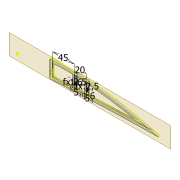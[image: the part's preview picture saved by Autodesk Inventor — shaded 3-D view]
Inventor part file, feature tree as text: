
AUTODESK INVENTOR PART (.ipt)
format: ipt  version: 2022 (Build 260153000, 153)  size: 321,536 bytes
history: native  units: mm
features: extrude x6, sketch x6, projected_geometry x4, shell x1, fillet x1, plane x1
ambient origin geometry x8: Origin, YZ Plane, XZ Plane, XY Plane, X Axis, Y Axis, Z Axis, Center Point
bodies: Solid1 (feature_tree)
feature tree (19):
  extrude  "Extrusion1"  Depth=5.0mm
  shell  "Shell1"  Thickness=6.0mm
  extrude  "Extrusion2"  Depth=2.0mm
  extrude  "Extrusion3"  Depth=5.9mm
  extrude  "Extrusion4"  Depth=10.0mm TaperAngle=0.0deg
  fillet  "Fillet1"  Radius=70.0mm
  plane  "Work Plane1"
  extrude  "Extrusion5"  Depth=4.0mm TaperAngle=0.0deg
  extrude  "Extrusion8"  Depth=0.5mm
  sketch  "Sketch3"  dims[d0=4.0mm d1=0.0mm d2=5.0mm d3=6.0mm]
  sketch  "Sketch7"  dims[d5=4.0mm d6=0.0mm d7=2.0mm]
  projected_geometry  "Projected Loop3"
  sketch  "Sketch8"  dims[d8=2.0mm d9=5.9mm]
  sketch  "Sketch9"  dims[d12=5.0mm d13=10.0mm d14=0.0mm d15=70.0mm]
  sketch  "Sketch10"  dims[d16=10.0mm d17=0.0mm d22=4.0mm d23=0.0mm]
  projected_geometry  "Projected Loop4"
  projected_geometry  "Projected Loop10"
  sketch  "Sketch16"  dims[d24=2.0mm d26=2.0mm d31=2.0mm d32=5.0mm d34=1.6mm d35=2.5mm d37=5.0mm d38=1.6mm d40=2.5mm d41=45.0mm d42=20.0mm d43=0.5mm d44=10.0mm d45=0.0mm]
  projected_geometry  "Projected Loop11"
